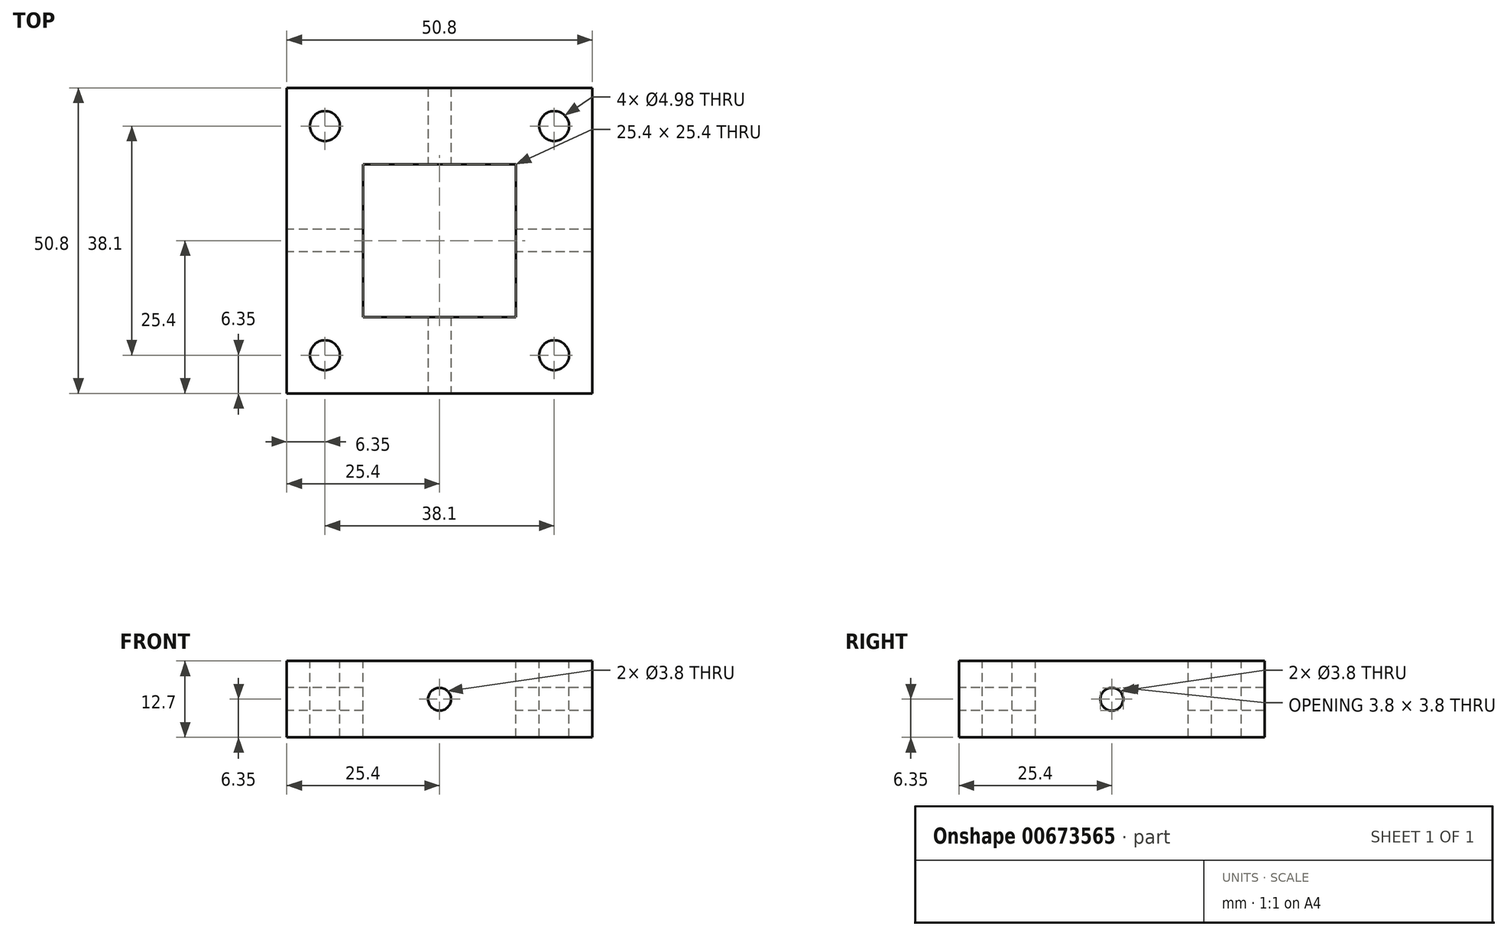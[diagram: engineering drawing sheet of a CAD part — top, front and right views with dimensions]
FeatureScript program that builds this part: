
annotation { "Feature Type Name" : "Feature", "Feature Type Description" : "" }
export const myFeature = defineFeature(function(context is Context, id is Id, definition is map)
    precondition{}
    {
        {
            var Q0;
            Q0=qCreatedBy(makeId("Top.planeOp"),FACE);
            var sketch = newSketch(context, id + "F0", { "sketchPlane" : qUnion([Q0])});
            skLineSegment(sketch, "E0.bottom", {"start": v(0, 0) * mm, "end": v(50.8, 0) * mm});
            skLineSegment(sketch, "E0.top", {"start": v(0, 50.8) * mm, "end": v(50.8, 50.8) * mm});
            skLineSegment(sketch, "E0.left", {"start": v(0, 0) * mm, "end": v(0, 50.8) * mm});
            skLineSegment(sketch, "E0.right", {"start": v(50.8, 0) * mm, "end": v(50.8, 50.8) * mm});
            skSolve(sketch);
        }
        {
            var Q0;
            Q0=makeQuery(id+"F0.imprint","IMPRINT",FACE,{"disambiguationData":[TD([[makeQuery(id+"F0.imprint","IMPRINT",EDGE,{"derivedFrom":sQuery(id+"F0.wireOp",EDGE,"E0.bottom")}),1.0]])]});
            extrude(context, id + "F1", {"entities" : qUnion([Q0]), "depth" : 6.35 * mm, "offsetDistance" : 25.4 * mm, "hasSecondDirection" : true, "secondDirectionOppositeDirection" : true, "secondDirectionDepth" : 6.35 * mm});
        }
        {
            var Q0;
            Q0=makeQuery(id+"F1.opExtrude","CAP_FACE",FACE,{"disambiguationData":[OSD([sQuery(id+"F0.wireOp",EDGE,"E0.bottom"),sQuery(id+"F0.wireOp",EDGE,"E0.top"),sQuery(id+"F0.wireOp",EDGE,"E0.left"),sQuery(id+"F0.wireOp",EDGE,"E0.right")])],"isStart":false});
            var sketch = newSketch(context, id + "F2", { "sketchPlane" : qUnion([Q0])});
            skLineSegment(sketch, "E1.0", {"start": v(38.1, 12.7) * mm, "end": v(38.1, 38.1) * mm});
            skLineSegment(sketch, "E1.1", {"start": v(12.7, 12.7) * mm, "end": v(38.1, 12.7) * mm});
            skLineSegment(sketch, "E1.2", {"start": v(12.7, 12.7) * mm, "end": v(12.7, 38.1) * mm});
            skLineSegment(sketch, "E1.3", {"start": v(12.7, 38.1) * mm, "end": v(38.1, 38.1) * mm});
            skLineSegment(sketch, "E2.0", {"start": v(44.45, 6.35) * mm, "end": v(44.45, 44.45) * mm, "construction": true});
            skLineSegment(sketch, "E2.1", {"start": v(6.35, 6.35) * mm, "end": v(44.45, 6.35) * mm, "construction": true});
            skLineSegment(sketch, "E2.2", {"start": v(6.35, 6.35) * mm, "end": v(6.35, 44.45) * mm, "construction": true});
            skLineSegment(sketch, "E2.3", {"start": v(6.35, 44.45) * mm, "end": v(44.45, 44.45) * mm, "construction": true});
            skSolve(sketch);
        }
        {
            var Q0;
            Q0=makeQuery(id+"F2.imprint","IMPRINT",FACE,{"disambiguationData":[TD([[makeQuery(id+"F2.imprint","IMPRINT",EDGE,{"derivedFrom":sQuery(id+"F2.wireOp",EDGE,"E1.0")}),1.0]])]});
            extrude(context, id + "F3", {"entities" : qUnion([Q0]), "operationType" : NewBodyOperationType.REMOVE, "oppositeDirection" : true, "depth" : 113.74 * mm, "offsetDistance" : 25.4 * mm});
        }
        {
            var Q0;
            Q0=sQuery(id+"F2.wireOp",VERTEX,"E2.0.end");
            var Q1;
            Q1=sQuery(id+"F2.wireOp",VERTEX,"E2.2.end");
            var Q2;
            Q2=sQuery(id+"F2.wireOp",VERTEX,"E2.2.start");
            var Q3;
            Q3=sQuery(id+"F2.wireOp",VERTEX,"E2.1.end");
            var Q4;
            Q4=makeQuery(id+"F1.opExtrude","SWEPT_BODY",BODY,{"disambiguationData":[OSD([sQuery(id+"F0.wireOp",EDGE,"E0.bottom"),sQuery(id+"F0.wireOp",EDGE,"E0.top"),sQuery(id+"F0.wireOp",EDGE,"E0.left"),sQuery(id+"F0.wireOp",EDGE,"E0.right")])]});
            hole(context, id + "F4", {"style" : HoleStyle.SIMPLE, "endStyle" : HoleEndStyle.THROUGH, "standardTappedOrClearance" : lookupTablePath({ "fit" : "Close", "standard" : "ANSI", "size" : "#10", "type" : "Clearance" }), "standardBlindInLast" : lookupTablePath({ "fit" : "Close", "standard" : "ANSI", "size" : "#10", "type" : "Clearance" }), "holeDiameter" : 4.98 * mm, "majorDiameter" : 6.35 * mm, "isTappedThrough" : true, "tappedDepth" : 12.7 * mm, "tapClearance" : 3, "locations" : qUnion([Q0, Q1, Q2, Q3]), "scope" : qUnion([Q4])});
        }
        {
            var Q0;
            Q0=makeQuery(id+"F1.opExtrude","SWEPT_FACE",FACE,{"disambiguationData":[OSD([sQuery(id+"F0.wireOp",EDGE,"E0.left")])]});
            var sketch = newSketch(context, id + "F5", { "sketchPlane" : qUnion([Q0])});
            skPoint(sketch, "E3", {"position": v(-25.4, 0) * mm});
            skPoint(sketch, "E4", {"position": v(-25.4, 6.35) * mm});
            skPoint(sketch, "E5", {"position": v(-50.8, 0) * mm});
            skSolve(sketch);
        }
        {
            var Q0;
            Q0=makeQuery(id+"F1.opExtrude","SWEPT_FACE",FACE,{"disambiguationData":[OSD([sQuery(id+"F0.wireOp",EDGE,"E0.bottom")])]});
            var sketch = newSketch(context, id + "F6", { "sketchPlane" : qUnion([Q0])});
            skPoint(sketch, "E6", {"position": v(25.4, 0) * mm});
            skPoint(sketch, "E7", {"position": v(25.4, 6.35) * mm});
            skPoint(sketch, "E8", {"position": v(0, 0) * mm});
            skSolve(sketch);
        }
        {
            var Q0;
            Q0=sQuery(id+"F6.wireOp",VERTEX,"E6");
            var Q1;
            Q1=sQuery(id+"F5.wireOp",VERTEX,"E3");
            var Q2;
            Q2=makeQuery(id+"F1.opExtrude","SWEPT_BODY",BODY,{"disambiguationData":[OSD([sQuery(id+"F0.wireOp",EDGE,"E0.bottom"),sQuery(id+"F0.wireOp",EDGE,"E0.top"),sQuery(id+"F0.wireOp",EDGE,"E0.left"),sQuery(id+"F0.wireOp",EDGE,"E0.right")])]});
            hole(context, id + "F7", {"style" : HoleStyle.SIMPLE, "endStyle" : HoleEndStyle.THROUGH, "standardTappedOrClearance" : lookupTablePath({ "fit" : "Normal (ASME)", "standard" : "ANSI", "engagement" : "75%", "pitch" : "24 tpi", "size" : "#10", "type" : "Tapped" }), "standardBlindInLast" : lookupTablePath({ "fit" : "Free", "standard" : "ANSI", "engagement" : "75%", "pitch" : "24 tpi", "size" : "#10", "type" : "Tapped" }), "holeDiameter" : 3.8 * mm, "majorDiameter" : 4.83 * mm, "showTappedDepth" : true, "isTappedThrough" : true, "tappedDepth" : 12.7 * mm, "tapClearance" : 3, "locations" : qUnion([Q0, Q1]), "scope" : qUnion([Q2])});
        }
    });
